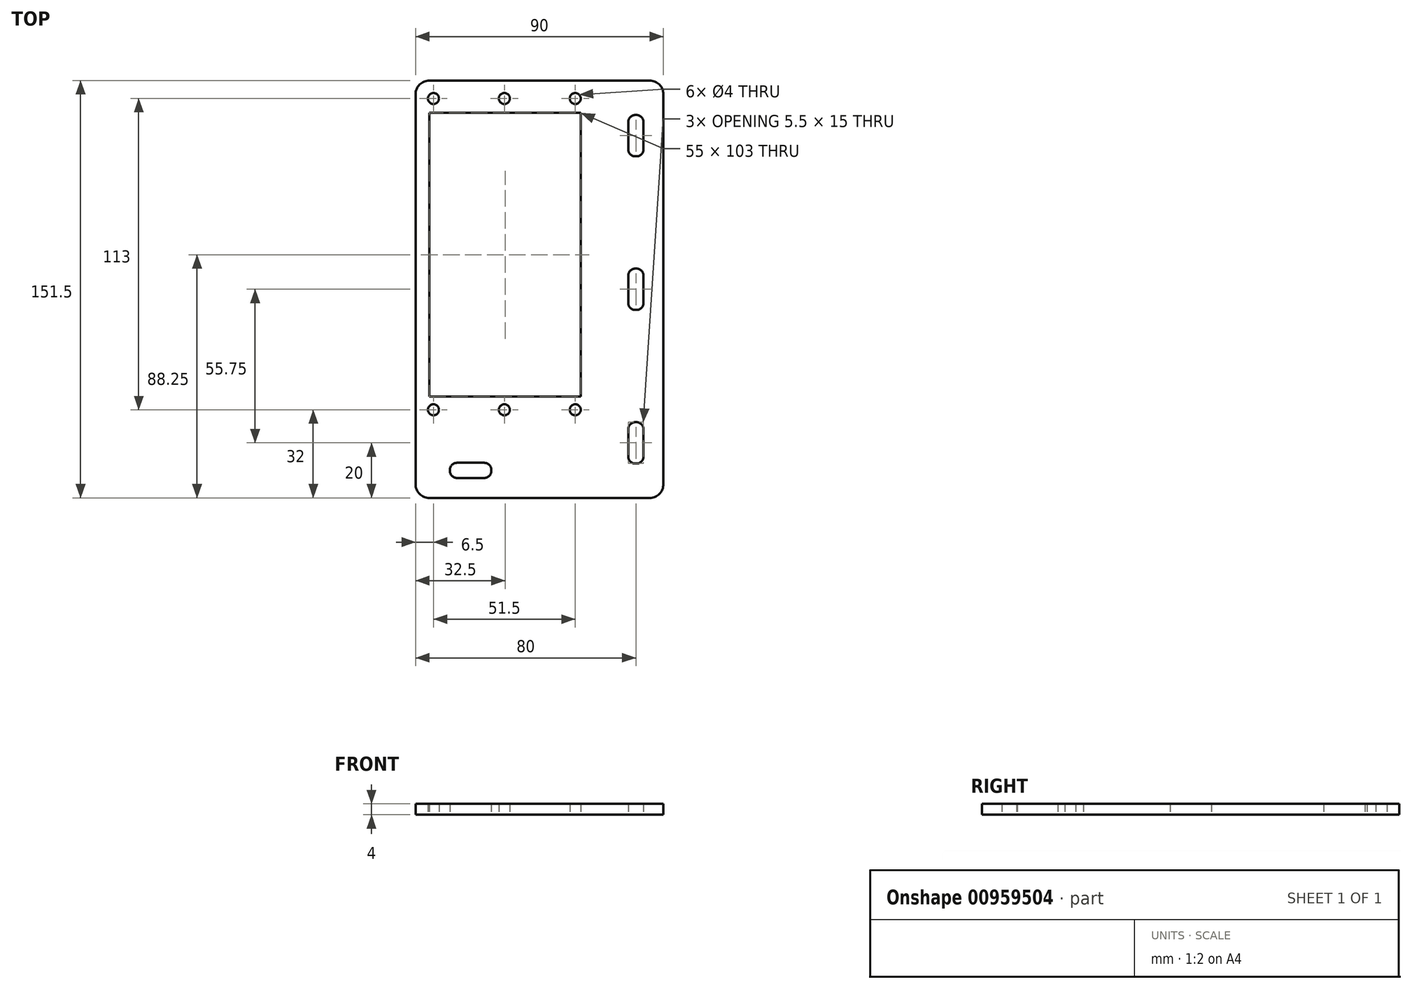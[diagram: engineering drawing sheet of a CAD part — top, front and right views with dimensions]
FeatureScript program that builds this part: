
annotation { "Feature Type Name" : "Feature", "Feature Type Description" : "" }
export const myFeature = defineFeature(function(context is Context, id is Id, definition is map)
    precondition{}
    {
        {
            var Q0;
            Q0=qCreatedBy(makeId("Top.planeOp"),FACE);
            var sketch = newSketch(context, id + "F0", { "sketchPlane" : qUnion([Q0])});
            skLineSegment(sketch, "E0.bottom", {"start": v(32.5, -63.25) * mm, "end": v(-32.5, -63.25) * mm, "construction": true});
            skLineSegment(sketch, "E0.top", {"start": v(32.5, 63.25) * mm, "end": v(-32.5, 63.25) * mm});
            skLineSegment(sketch, "E0.left", {"start": v(32.5, -63.25) * mm, "end": v(32.5, 63.25) * mm, "construction": true});
            skLineSegment(sketch, "E0.right", {"start": v(-32.5, -63.25) * mm, "end": v(-32.5, 63.25) * mm});
            skPoint(sketch, "E0.middle", {"position": v(0, 0) * mm});
            skLineSegment(sketch, "E1", {"start": v(32.5, 63.25) * mm, "end": v(57.5, 63.25) * mm});
            skLineSegment(sketch, "E2", {"start": v(57.5, -88.25) * mm, "end": v(57.5, 63.25) * mm});
            skLineSegment(sketch, "E3", {"start": v(57.5, -88.25) * mm, "end": v(-32.5, -88.25) * mm});
            skLineSegment(sketch, "E4", {"start": v(-32.5, -88.25) * mm, "end": v(-32.5, -63.25) * mm});
            skLineSegment(sketch, "E5", {"start": v(47.5, 63.25) * mm, "end": v(47.5, -88.25) * mm, "construction": true});
            skLineSegment(sketch, "E6", {"start": v(-32.5, -78.25) * mm, "end": v(57.5, -78.25) * mm, "construction": true});
            skLineSegment(sketch, "E7", {"start": v(0, 63.25) * mm, "end": v(0, -63.25) * mm, "construction": true});
            skLineSegment(sketch, "E8", {"start": v(-26, -56.25) * mm, "end": v(25.5, -56.25) * mm, "construction": true});
            skLineSegment(sketch, "E9", {"start": v(-26, 56.75) * mm, "end": v(25.5, 56.75) * mm, "construction": true});
            skPoint(sketch, "E10", {"position": v(-0.25, 56.75) * mm});
            skPoint(sketch, "E11", {"position": v(-0.25, -56.25) * mm});
            skLineSegment(sketch, "E12", {"start": v(-0.25, 56.75) * mm, "end": v(-0.25, -56.25) * mm, "construction": true});
            skCircle(sketch, "E13", {"center": v(-26, 56.75) * mm, "radius": 2 * mm});
            skCircle(sketch, "E14", {"center": v(-0.25, 56.75) * mm, "radius": 2 * mm});
            skCircle(sketch, "E15", {"center": v(25.5, 56.75) * mm, "radius": 2 * mm});
            skCircle(sketch, "E16", {"center": v(25.5, -56.25) * mm, "radius": 2 * mm});
            skCircle(sketch, "E17", {"center": v(-0.25, -56.25) * mm, "radius": 2 * mm});
            skCircle(sketch, "E18", {"center": v(-26, -56.25) * mm, "radius": 2 * mm});
            skLineSegment(sketch, "E19.bottom", {"start": v(27.5, -51.5) * mm, "end": v(-27.5, -51.5) * mm});
            skLineSegment(sketch, "E19.top", {"start": v(27.5, 51.5) * mm, "end": v(-27.5, 51.5) * mm});
            skLineSegment(sketch, "E19.left", {"start": v(27.5, -51.5) * mm, "end": v(27.5, 51.5) * mm});
            skLineSegment(sketch, "E19.right", {"start": v(-27.5, -51.5) * mm, "end": v(-27.5, 51.5) * mm});
            skLineSegment(sketch, "E20.bottom", {"start": v(-5, -81) * mm, "end": v(-20, -81) * mm});
            skLineSegment(sketch, "E20.top", {"start": v(-5, -75.5) * mm, "end": v(-20, -75.5) * mm});
            skLineSegment(sketch, "E20.left", {"start": v(-5, -81) * mm, "end": v(-5, -75.5) * mm});
            skLineSegment(sketch, "E20.right", {"start": v(-20, -81) * mm, "end": v(-20, -75.5) * mm});
            skPoint(sketch, "E20.middle", {"position": v(-12.5, -78.25) * mm});
            skLineSegment(sketch, "E21.bottom", {"start": v(44.75, 35.75) * mm, "end": v(50.25, 35.75) * mm});
            skLineSegment(sketch, "E21.top", {"start": v(44.75, 50.75) * mm, "end": v(50.25, 50.75) * mm});
            skLineSegment(sketch, "E21.left", {"start": v(44.75, 35.75) * mm, "end": v(44.75, 50.75) * mm});
            skLineSegment(sketch, "E21.right", {"start": v(50.25, 35.75) * mm, "end": v(50.25, 50.75) * mm});
            skPoint(sketch, "E21.middle", {"position": v(47.5, 43.25) * mm});
            skLineSegment(sketch, "E22.bottom", {"start": v(44.75, -20) * mm, "end": v(50.25, -20) * mm});
            skLineSegment(sketch, "E22.top", {"start": v(44.75, -5) * mm, "end": v(50.25, -5) * mm});
            skLineSegment(sketch, "E22.left", {"start": v(44.75, -20) * mm, "end": v(44.75, -5) * mm});
            skLineSegment(sketch, "E22.right", {"start": v(50.25, -20) * mm, "end": v(50.25, -5) * mm});
            skPoint(sketch, "E22.middle", {"position": v(47.5, -12.5) * mm});
            skLineSegment(sketch, "E23.bottom", {"start": v(44.75, -75.75) * mm, "end": v(50.25, -75.75) * mm});
            skLineSegment(sketch, "E23.top", {"start": v(44.75, -60.75) * mm, "end": v(50.25, -60.75) * mm});
            skLineSegment(sketch, "E23.left", {"start": v(44.75, -75.75) * mm, "end": v(44.75, -60.75) * mm});
            skLineSegment(sketch, "E23.right", {"start": v(50.25, -75.75) * mm, "end": v(50.25, -60.75) * mm});
            skPoint(sketch, "E23.middle", {"position": v(47.5, -68.25) * mm});
            skLineSegment(sketch, "E24", {"start": v(27.5, 0) * mm, "end": v(57.5, 0) * mm, "construction": true});
            skSolve(sketch);
        }
        {
            var Q0;
            Q0 = qSketchRegion(id + "F0", true);
            extrude(context, id + "F1", {"entities" : qUnion([Q0]), "depth" : 4 * mm, "offsetDistance" : 25 * mm});
        }
        {
            var Q0;
            Q0=makeQuery(id+"F1.opExtrude","SWEPT_EDGE",EDGE,{"disambiguationData":[OSD([sQuery(id+"F0.wireOp",EDGE,"E20.bottom"),sQuery(id+"F0.wireOp",EDGE,"E20.right")])]});
            var Q1;
            Q1=makeQuery(id+"F1.opExtrude","SWEPT_EDGE",EDGE,{"disambiguationData":[OSD([sQuery(id+"F0.wireOp",EDGE,"E20.top"),sQuery(id+"F0.wireOp",EDGE,"E20.right")])]});
            var Q2;
            Q2=makeQuery(id+"F1.opExtrude","SWEPT_EDGE",EDGE,{"disambiguationData":[OSD([sQuery(id+"F0.wireOp",EDGE,"E20.top"),sQuery(id+"F0.wireOp",EDGE,"E20.left")])]});
            var Q3;
            Q3=makeQuery(id+"F1.opExtrude","SWEPT_EDGE",EDGE,{"disambiguationData":[OSD([sQuery(id+"F0.wireOp",EDGE,"E20.bottom"),sQuery(id+"F0.wireOp",EDGE,"E20.left")])]});
            var Q4;
            Q4=makeQuery(id+"F1.opExtrude","SWEPT_EDGE",EDGE,{"disambiguationData":[OSD([sQuery(id+"F0.wireOp",EDGE,"3TRtV0j2-0wF1-ATcU-z3Ki-uDWPs8kBkXXh.bottom"),sQuery(id+"F0.wireOp",EDGE,"3TRtV0j2-0wF1-ATcU-z3Ki-uDWPs8kBkXXh.left")])]});
            var Q5;
            Q5=makeQuery(id+"F1.opExtrude","SWEPT_EDGE",EDGE,{"disambiguationData":[OSD([sQuery(id+"F0.wireOp",EDGE,"3TRtV0j2-0wF1-ATcU-z3Ki-uDWPs8kBkXXh.top"),sQuery(id+"F0.wireOp",EDGE,"3TRtV0j2-0wF1-ATcU-z3Ki-uDWPs8kBkXXh.left")])]});
            var Q6;
            Q6=makeQuery(id+"F1.opExtrude","SWEPT_EDGE",EDGE,{"disambiguationData":[OSD([sQuery(id+"F0.wireOp",EDGE,"3TRtV0j2-0wF1-ATcU-z3Ki-uDWPs8kBkXXh.top"),sQuery(id+"F0.wireOp",EDGE,"3TRtV0j2-0wF1-ATcU-z3Ki-uDWPs8kBkXXh.right")])]});
            var Q7;
            Q7=makeQuery(id+"F1.opExtrude","SWEPT_EDGE",EDGE,{"disambiguationData":[OSD([sQuery(id+"F0.wireOp",EDGE,"3TRtV0j2-0wF1-ATcU-z3Ki-uDWPs8kBkXXh.bottom"),sQuery(id+"F0.wireOp",EDGE,"3TRtV0j2-0wF1-ATcU-z3Ki-uDWPs8kBkXXh.right")])]});
            var Q8;
            Q8=makeQuery(id+"F1.opExtrude","SWEPT_EDGE",EDGE,{"disambiguationData":[OSD([sQuery(id+"F0.wireOp",EDGE,"E23.top"),sQuery(id+"F0.wireOp",EDGE,"E23.right")])]});
            var Q9;
            Q9=makeQuery(id+"F1.opExtrude","SWEPT_EDGE",EDGE,{"disambiguationData":[OSD([sQuery(id+"F0.wireOp",EDGE,"E23.bottom"),sQuery(id+"F0.wireOp",EDGE,"E23.right")])]});
            var Q10;
            Q10=makeQuery(id+"F1.opExtrude","SWEPT_EDGE",EDGE,{"disambiguationData":[OSD([sQuery(id+"F0.wireOp",EDGE,"E23.bottom"),sQuery(id+"F0.wireOp",EDGE,"E23.left")])]});
            var Q11;
            Q11=makeQuery(id+"F1.opExtrude","SWEPT_EDGE",EDGE,{"disambiguationData":[OSD([sQuery(id+"F0.wireOp",EDGE,"E23.top"),sQuery(id+"F0.wireOp",EDGE,"E23.left")])]});
            var Q12;
            Q12=makeQuery(id+"F1.opExtrude","SWEPT_EDGE",EDGE,{"disambiguationData":[OSD([sQuery(id+"F0.wireOp",EDGE,"E22.top"),sQuery(id+"F0.wireOp",EDGE,"E22.left")])]});
            var Q13;
            Q13=makeQuery(id+"F1.opExtrude","SWEPT_EDGE",EDGE,{"disambiguationData":[OSD([sQuery(id+"F0.wireOp",EDGE,"E22.top"),sQuery(id+"F0.wireOp",EDGE,"E22.right")])]});
            var Q14;
            Q14=makeQuery(id+"F1.opExtrude","SWEPT_EDGE",EDGE,{"disambiguationData":[OSD([sQuery(id+"F0.wireOp",EDGE,"E22.bottom"),sQuery(id+"F0.wireOp",EDGE,"E22.right")])]});
            var Q15;
            Q15=makeQuery(id+"F1.opExtrude","SWEPT_EDGE",EDGE,{"disambiguationData":[OSD([sQuery(id+"F0.wireOp",EDGE,"E22.bottom"),sQuery(id+"F0.wireOp",EDGE,"E22.left")])]});
            var Q16;
            Q16=makeQuery(id+"F1.opExtrude","SWEPT_EDGE",EDGE,{"disambiguationData":[OSD([sQuery(id+"F0.wireOp",EDGE,"E21.bottom"),sQuery(id+"F0.wireOp",EDGE,"E21.left")])]});
            var Q17;
            Q17=makeQuery(id+"F1.opExtrude","SWEPT_EDGE",EDGE,{"disambiguationData":[OSD([sQuery(id+"F0.wireOp",EDGE,"E21.top"),sQuery(id+"F0.wireOp",EDGE,"E21.left")])]});
            var Q18;
            Q18=makeQuery(id+"F1.opExtrude","SWEPT_EDGE",EDGE,{"disambiguationData":[OSD([sQuery(id+"F0.wireOp",EDGE,"E21.top"),sQuery(id+"F0.wireOp",EDGE,"E21.right")])]});
            var Q19;
            Q19=makeQuery(id+"F1.opExtrude","SWEPT_EDGE",EDGE,{"disambiguationData":[OSD([sQuery(id+"F0.wireOp",EDGE,"E21.bottom"),sQuery(id+"F0.wireOp",EDGE,"E21.right")])]});
            fillet(context, id + "F2", {"entities" : qUnion([Q0, Q1, Q2, Q3, Q4, Q5, Q6, Q7, Q8, Q9, Q10, Q11, Q12, Q13, Q14, Q15, Q16, Q17, Q18, Q19]), "radius" : 2.5 * mm, "tangentPropagation" : true, "allowEdgeOverflow" : false});
        }
        {
            var Q0;
            Q0=makeQuery(id+"F1.opExtrude","SWEPT_EDGE",EDGE,{"disambiguationData":[OSD([sQuery(id+"F0.wireOp",EDGE,"E0.top"),sQuery(id+"F0.wireOp",EDGE,"E0.right")])]});
            var Q1;
            Q1=makeQuery(id+"F1.opExtrude","SWEPT_EDGE",EDGE,{"disambiguationData":[OSD([sQuery(id+"F0.wireOp",EDGE,"E3"),sQuery(id+"F0.wireOp",EDGE,"E4")])]});
            var Q2;
            Q2=makeQuery(id+"F1.opExtrude","SWEPT_EDGE",EDGE,{"disambiguationData":[OSD([sQuery(id+"F0.wireOp",EDGE,"E2"),sQuery(id+"F0.wireOp",EDGE,"E3")])]});
            var Q3;
            Q3=makeQuery(id+"F1.opExtrude","SWEPT_EDGE",EDGE,{"disambiguationData":[OSD([sQuery(id+"F0.wireOp",EDGE,"E1"),sQuery(id+"F0.wireOp",EDGE,"E2")])]});
            fillet(context, id + "F3", {"entities" : qUnion([Q0, Q1, Q2, Q3]), "radius" : 5 * mm, "tangentPropagation" : true, "allowEdgeOverflow" : false});
        }
    });
